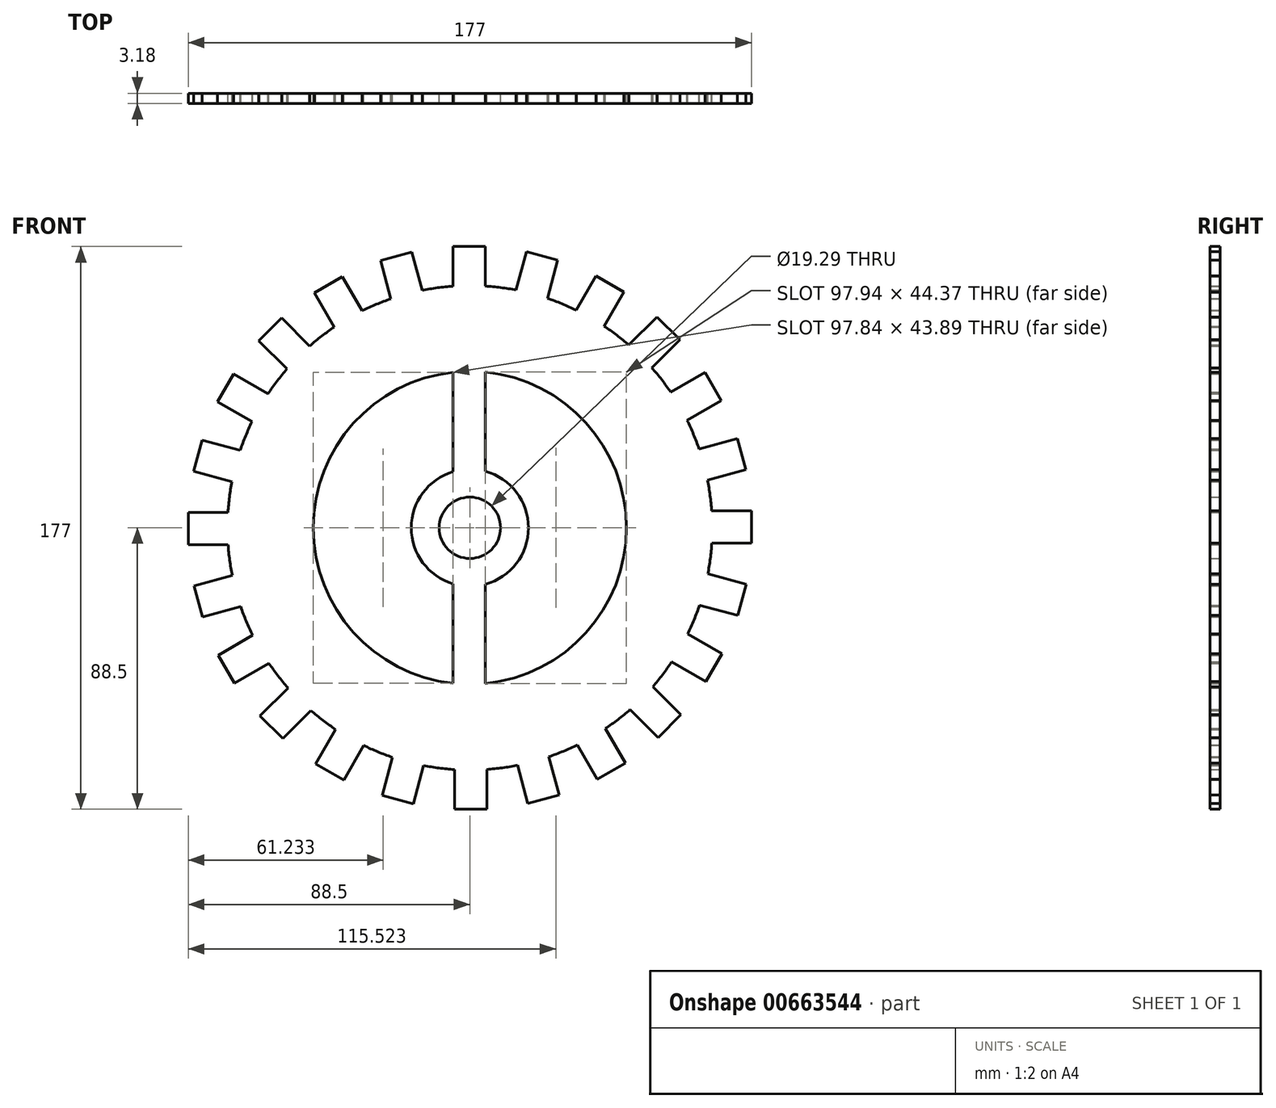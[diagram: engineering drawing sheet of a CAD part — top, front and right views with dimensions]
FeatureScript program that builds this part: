
annotation { "Feature Type Name" : "Feature", "Feature Type Description" : "" }
export const myFeature = defineFeature(function(context is Context, id is Id, definition is map)
    precondition{}
    {
        {
            var Q0;
            Q0=qCreatedBy(makeId("Front.planeOp"),FACE);
            var sketch = newSketch(context, id + "F0", { "sketchPlane" : qUnion([Q0])});
            skCircle(sketch, "E0", {"center": v(0, 0) * mm, "radius": 76.2 * mm, "construction": true});
            skLineSegment(sketch, "E1", {"start": v(-5.32, 76.01) * mm, "end": v(-5.32, 88.5) * mm});
            skLineSegment(sketch, "E2", {"start": v(-5.32, 88.5) * mm, "end": v(4.84, 88.5) * mm});
            skLineSegment(sketch, "E3", {"start": v(4.84, 88.5) * mm, "end": v(4.84, 76.05) * mm});
            skLineSegment(sketch, "E4.1.0", {"start": v(-24.82, 72.05) * mm, "end": v(-28.05, 84.1) * mm});
            skLineSegment(sketch, "E4.1.1", {"start": v(-28.05, 84.1) * mm, "end": v(-18.23, 86.74) * mm});
            skLineSegment(sketch, "E4.1.2", {"start": v(-18.23, 86.74) * mm, "end": v(-15.01, 74.7) * mm});
            skLineSegment(sketch, "E4.2.0", {"start": v(-42.62, 63.17) * mm, "end": v(-48.86, 73.98) * mm});
            skLineSegment(sketch, "E4.2.1", {"start": v(-48.86, 73.98) * mm, "end": v(-40.06, 79.06) * mm});
            skLineSegment(sketch, "E4.2.2", {"start": v(-40.06, 79.06) * mm, "end": v(-33.83, 68.28) * mm});
            skLineSegment(sketch, "E4.3.0", {"start": v(-57.51, 49.99) * mm, "end": v(-66.34, 58.82) * mm});
            skLineSegment(sketch, "E4.3.1", {"start": v(-66.34, 58.82) * mm, "end": v(-59.16, 66) * mm});
            skLineSegment(sketch, "E4.3.2", {"start": v(-59.16, 66) * mm, "end": v(-50.35, 57.2) * mm});
            skLineSegment(sketch, "E4.4.0", {"start": v(-68.5, 33.4) * mm, "end": v(-79.3, 39.64) * mm});
            skLineSegment(sketch, "E4.4.1", {"start": v(-79.3, 39.64) * mm, "end": v(-74.23, 48.44) * mm});
            skLineSegment(sketch, "E4.4.2", {"start": v(-74.23, 48.44) * mm, "end": v(-63.44, 42.21) * mm});
            skLineSegment(sketch, "E4.5.0", {"start": v(-74.8, 14.53) * mm, "end": v(-86.86, 17.76) * mm});
            skLineSegment(sketch, "E4.5.1", {"start": v(-86.86, 17.76) * mm, "end": v(-84.23, 27.58) * mm});
            skLineSegment(sketch, "E4.5.2", {"start": v(-84.23, 27.58) * mm, "end": v(-72.2, 24.35) * mm});
            skLineSegment(sketch, "E4.6.0", {"start": v(-76.01, -5.32) * mm, "end": v(-88.5, -5.32) * mm});
            skLineSegment(sketch, "E4.6.1", {"start": v(-88.5, -5.32) * mm, "end": v(-88.5, 4.84) * mm});
            skLineSegment(sketch, "E4.6.2", {"start": v(-88.5, 4.84) * mm, "end": v(-76.05, 4.84) * mm});
            skLineSegment(sketch, "E4.7.0", {"start": v(-72.05, -24.82) * mm, "end": v(-84.1, -28.05) * mm});
            skLineSegment(sketch, "E4.7.1", {"start": v(-84.1, -28.05) * mm, "end": v(-86.74, -18.23) * mm});
            skLineSegment(sketch, "E4.7.2", {"start": v(-86.74, -18.23) * mm, "end": v(-74.7, -15.01) * mm});
            skLineSegment(sketch, "E4.8.0", {"start": v(-63.17, -42.62) * mm, "end": v(-73.98, -48.86) * mm});
            skLineSegment(sketch, "E4.8.1", {"start": v(-73.98, -48.86) * mm, "end": v(-79.06, -40.06) * mm});
            skLineSegment(sketch, "E4.8.2", {"start": v(-79.06, -40.06) * mm, "end": v(-68.28, -33.83) * mm});
            skLineSegment(sketch, "E4.9.0", {"start": v(-49.99, -57.51) * mm, "end": v(-58.82, -66.34) * mm});
            skLineSegment(sketch, "E4.9.1", {"start": v(-58.82, -66.34) * mm, "end": v(-66, -59.16) * mm});
            skLineSegment(sketch, "E4.9.2", {"start": v(-66, -59.16) * mm, "end": v(-57.2, -50.35) * mm});
            skLineSegment(sketch, "E4.10.0", {"start": v(-33.4, -68.5) * mm, "end": v(-39.64, -79.3) * mm});
            skLineSegment(sketch, "E4.10.1", {"start": v(-39.64, -79.3) * mm, "end": v(-48.44, -74.23) * mm});
            skLineSegment(sketch, "E4.10.2", {"start": v(-48.44, -74.23) * mm, "end": v(-42.21, -63.44) * mm});
            skLineSegment(sketch, "E4.11.0", {"start": v(-14.53, -74.8) * mm, "end": v(-17.76, -86.86) * mm});
            skLineSegment(sketch, "E4.11.1", {"start": v(-17.76, -86.86) * mm, "end": v(-27.58, -84.23) * mm});
            skLineSegment(sketch, "E4.11.2", {"start": v(-27.58, -84.23) * mm, "end": v(-24.35, -72.2) * mm});
            skLineSegment(sketch, "E4.12.0", {"start": v(5.32, -76.01) * mm, "end": v(5.32, -88.5) * mm});
            skLineSegment(sketch, "E4.12.1", {"start": v(5.32, -88.5) * mm, "end": v(-4.84, -88.5) * mm});
            skLineSegment(sketch, "E4.12.2", {"start": v(-4.84, -88.5) * mm, "end": v(-4.84, -76.05) * mm});
            skLineSegment(sketch, "E4.13.0", {"start": v(24.82, -72.05) * mm, "end": v(28.05, -84.1) * mm});
            skLineSegment(sketch, "E4.13.1", {"start": v(28.05, -84.1) * mm, "end": v(18.23, -86.74) * mm});
            skLineSegment(sketch, "E4.13.2", {"start": v(18.23, -86.74) * mm, "end": v(15.01, -74.7) * mm});
            skLineSegment(sketch, "E4.14.0", {"start": v(42.62, -63.17) * mm, "end": v(48.86, -73.98) * mm});
            skLineSegment(sketch, "E4.14.1", {"start": v(48.86, -73.98) * mm, "end": v(40.06, -79.06) * mm});
            skLineSegment(sketch, "E4.14.2", {"start": v(40.06, -79.06) * mm, "end": v(33.83, -68.28) * mm});
            skLineSegment(sketch, "E4.15.0", {"start": v(57.51, -49.99) * mm, "end": v(66.34, -58.82) * mm});
            skLineSegment(sketch, "E4.15.1", {"start": v(66.34, -58.82) * mm, "end": v(59.16, -66) * mm});
            skLineSegment(sketch, "E4.15.2", {"start": v(59.16, -66) * mm, "end": v(50.35, -57.2) * mm});
            skLineSegment(sketch, "E4.16.0", {"start": v(68.5, -33.4) * mm, "end": v(79.3, -39.64) * mm});
            skLineSegment(sketch, "E4.16.1", {"start": v(79.3, -39.64) * mm, "end": v(74.23, -48.44) * mm});
            skLineSegment(sketch, "E4.16.2", {"start": v(74.23, -48.44) * mm, "end": v(63.44, -42.21) * mm});
            skLineSegment(sketch, "E4.17.0", {"start": v(74.8, -14.53) * mm, "end": v(86.86, -17.76) * mm});
            skLineSegment(sketch, "E4.17.1", {"start": v(86.86, -17.76) * mm, "end": v(84.23, -27.58) * mm});
            skLineSegment(sketch, "E4.17.2", {"start": v(84.23, -27.58) * mm, "end": v(72.2, -24.35) * mm});
            skLineSegment(sketch, "E4.18.0", {"start": v(76.01, 5.32) * mm, "end": v(88.5, 5.32) * mm});
            skLineSegment(sketch, "E4.18.1", {"start": v(88.5, 5.32) * mm, "end": v(88.5, -4.84) * mm});
            skLineSegment(sketch, "E4.18.2", {"start": v(88.5, -4.84) * mm, "end": v(76.05, -4.84) * mm});
            skLineSegment(sketch, "E4.19.0", {"start": v(72.05, 24.82) * mm, "end": v(84.1, 28.05) * mm});
            skLineSegment(sketch, "E4.19.1", {"start": v(84.1, 28.05) * mm, "end": v(86.74, 18.23) * mm});
            skLineSegment(sketch, "E4.19.2", {"start": v(86.74, 18.23) * mm, "end": v(74.7, 15.01) * mm});
            skLineSegment(sketch, "E4.20.0", {"start": v(63.17, 42.62) * mm, "end": v(73.98, 48.86) * mm});
            skLineSegment(sketch, "E4.20.1", {"start": v(73.98, 48.86) * mm, "end": v(79.06, 40.06) * mm});
            skLineSegment(sketch, "E4.20.2", {"start": v(79.06, 40.06) * mm, "end": v(68.28, 33.83) * mm});
            skLineSegment(sketch, "E4.21.0", {"start": v(49.99, 57.51) * mm, "end": v(58.82, 66.34) * mm});
            skLineSegment(sketch, "E4.21.1", {"start": v(58.82, 66.34) * mm, "end": v(66, 59.16) * mm});
            skLineSegment(sketch, "E4.21.2", {"start": v(66, 59.16) * mm, "end": v(57.2, 50.35) * mm});
            skLineSegment(sketch, "E4.22.0", {"start": v(33.4, 68.5) * mm, "end": v(39.64, 79.3) * mm});
            skLineSegment(sketch, "E4.22.1", {"start": v(39.64, 79.3) * mm, "end": v(48.44, 74.23) * mm});
            skLineSegment(sketch, "E4.22.2", {"start": v(48.44, 74.23) * mm, "end": v(42.21, 63.44) * mm});
            skLineSegment(sketch, "E4.23.0", {"start": v(14.53, 74.8) * mm, "end": v(17.76, 86.86) * mm});
            skLineSegment(sketch, "E4.23.1", {"start": v(17.76, 86.86) * mm, "end": v(27.58, 84.23) * mm});
            skLineSegment(sketch, "E4.23.2", {"start": v(27.58, 84.23) * mm, "end": v(24.35, 72.2) * mm});
            skCircle(sketch, "E5", {"center": v(0, 0) * mm, "radius": 18.42 * mm});
            skCircle(sketch, "E6", {"center": v(0, 0) * mm, "radius": 49.2 * mm});
            skCircle(sketch, "E7", {"center": v(0, 0) * mm, "radius": 76.2 * mm});
            skLineSegment(sketch, "E8", {"start": v(-5.32, 48.92) * mm, "end": v(-5.32, 17.63) * mm});
            skLineSegment(sketch, "E9", {"start": v(4.84, 48.97) * mm, "end": v(4.84, 17.77) * mm});
            skLineSegment(sketch, "E10", {"start": v(-5.32, -17.63) * mm, "end": v(-5.32, -48.92) * mm});
            skLineSegment(sketch, "E11", {"start": v(4.84, -17.77) * mm, "end": v(4.84, -48.97) * mm});
            skCircle(sketch, "E12", {"center": v(0, 0) * mm, "radius": 9.65 * mm});
            skSolve(sketch);
        }
        {
            var Q0;
            {var subQ0=sQuery(id+"F0.wireOp",EDGE,"E5");var subQ1=makeQuery(id+"F0.imprint","INTERSECT",VERTEX,{"derivedFrom":[subQ0,sQuery(id+"F0.wireOp",EDGE,"E8")]});Q0=makeQuery(id+"F0.imprint","IMPRINT",FACE,{"disambiguationData":[TD([[makeQuery(id+"F0.imprint","IMPRINT",EDGE,{"disambiguationData":[TD([[subQ1,1.0]])],"derivedFrom":subQ0}),1.0]])]});}
            var Q1;
            {var subQ0=sQuery(id+"F0.wireOp",EDGE,"E8");Q1=makeQuery(id+"F0.imprint","IMPRINT",FACE,{"disambiguationData":[TD([[makeQuery(id+"F0.imprint","IMPRINT",EDGE,{"derivedFrom":subQ0}),1.0]])]});}
            var Q2;
            {var subQ0=sQuery(id+"F0.wireOp",EDGE,"E10");Q2=makeQuery(id+"F0.imprint","IMPRINT",FACE,{"disambiguationData":[TD([[makeQuery(id+"F0.imprint","IMPRINT",EDGE,{"derivedFrom":subQ0}),1.0]])]});}
            var Q3;
            {var subQ33=sQuery(id+"F0.wireOp",EDGE,"E6");var subQ34=makeQuery(id+"F0.imprint","INTERSECT",VERTEX,{"derivedFrom":[subQ33,sQuery(id+"F0.wireOp",EDGE,"E8")]});Q3=makeQuery(id+"F0.imprint","IMPRINT",FACE,{"disambiguationData":[TD([[makeQuery(id+"F0.imprint","IMPRINT",EDGE,{"disambiguationData":[TD([[subQ34,1.0]])],"derivedFrom":subQ33}),-1.0]])]});}
            var Q4;
            {var subQ0=sQuery(id+"F0.wireOp",EDGE,"E4.12.0");Q4=makeQuery(id+"F0.imprint","IMPRINT",FACE,{"disambiguationData":[TD([[makeQuery(id+"F0.imprint","IMPRINT",EDGE,{"derivedFrom":subQ0}),-1.0]])]});}
            var Q5;
            {var subQ0=sQuery(id+"F0.wireOp",EDGE,"E4.13.0");Q5=makeQuery(id+"F0.imprint","IMPRINT",FACE,{"disambiguationData":[TD([[makeQuery(id+"F0.imprint","IMPRINT",EDGE,{"derivedFrom":subQ0}),-1.0]])]});}
            var Q6;
            {var subQ0=sQuery(id+"F0.wireOp",EDGE,"E4.14.0");Q6=makeQuery(id+"F0.imprint","IMPRINT",FACE,{"disambiguationData":[TD([[makeQuery(id+"F0.imprint","IMPRINT",EDGE,{"derivedFrom":subQ0}),-1.0]])]});}
            var Q7;
            {var subQ0=sQuery(id+"F0.wireOp",EDGE,"E4.15.0");Q7=makeQuery(id+"F0.imprint","IMPRINT",FACE,{"disambiguationData":[TD([[makeQuery(id+"F0.imprint","IMPRINT",EDGE,{"derivedFrom":subQ0}),-1.0]])]});}
            var Q8;
            {var subQ0=sQuery(id+"F0.wireOp",EDGE,"E4.16.0");Q8=makeQuery(id+"F0.imprint","IMPRINT",FACE,{"disambiguationData":[TD([[makeQuery(id+"F0.imprint","IMPRINT",EDGE,{"derivedFrom":subQ0}),-1.0]])]});}
            var Q9;
            {var subQ0=sQuery(id+"F0.wireOp",EDGE,"E4.17.0");Q9=makeQuery(id+"F0.imprint","IMPRINT",FACE,{"disambiguationData":[TD([[makeQuery(id+"F0.imprint","IMPRINT",EDGE,{"derivedFrom":subQ0}),-1.0]])]});}
            var Q10;
            {var subQ0=sQuery(id+"F0.wireOp",EDGE,"E4.18.0");Q10=makeQuery(id+"F0.imprint","IMPRINT",FACE,{"disambiguationData":[TD([[makeQuery(id+"F0.imprint","IMPRINT",EDGE,{"derivedFrom":subQ0}),-1.0]])]});}
            var Q11;
            {var subQ0=sQuery(id+"F0.wireOp",EDGE,"E4.19.0");Q11=makeQuery(id+"F0.imprint","IMPRINT",FACE,{"disambiguationData":[TD([[makeQuery(id+"F0.imprint","IMPRINT",EDGE,{"derivedFrom":subQ0}),-1.0]])]});}
            var Q12;
            {var subQ0=sQuery(id+"F0.wireOp",EDGE,"E4.20.0");Q12=makeQuery(id+"F0.imprint","IMPRINT",FACE,{"disambiguationData":[TD([[makeQuery(id+"F0.imprint","IMPRINT",EDGE,{"derivedFrom":subQ0}),-1.0]])]});}
            var Q13;
            {var subQ0=sQuery(id+"F0.wireOp",EDGE,"E4.22.0");Q13=makeQuery(id+"F0.imprint","IMPRINT",FACE,{"disambiguationData":[TD([[makeQuery(id+"F0.imprint","IMPRINT",EDGE,{"derivedFrom":subQ0}),-1.0]])]});}
            var Q14;
            {var subQ0=sQuery(id+"F0.wireOp",EDGE,"E4.23.0");Q14=makeQuery(id+"F0.imprint","IMPRINT",FACE,{"disambiguationData":[TD([[makeQuery(id+"F0.imprint","IMPRINT",EDGE,{"derivedFrom":subQ0}),-1.0]])]});}
            var Q15;
            {var subQ0=sQuery(id+"F0.wireOp",EDGE,"E4.21.0");Q15=makeQuery(id+"F0.imprint","IMPRINT",FACE,{"disambiguationData":[TD([[makeQuery(id+"F0.imprint","IMPRINT",EDGE,{"derivedFrom":subQ0}),-1.0]])]});}
            var Q16;
            {var subQ0=sQuery(id+"F0.wireOp",EDGE,"E1");Q16=makeQuery(id+"F0.imprint","IMPRINT",FACE,{"disambiguationData":[TD([[makeQuery(id+"F0.imprint","IMPRINT",EDGE,{"derivedFrom":subQ0}),-1.0]])]});}
            var Q17;
            {var subQ0=sQuery(id+"F0.wireOp",EDGE,"E4.1.0");Q17=makeQuery(id+"F0.imprint","IMPRINT",FACE,{"disambiguationData":[TD([[makeQuery(id+"F0.imprint","IMPRINT",EDGE,{"derivedFrom":subQ0}),-1.0]])]});}
            var Q18;
            {var subQ0=sQuery(id+"F0.wireOp",EDGE,"E4.2.0");Q18=makeQuery(id+"F0.imprint","IMPRINT",FACE,{"disambiguationData":[TD([[makeQuery(id+"F0.imprint","IMPRINT",EDGE,{"derivedFrom":subQ0}),-1.0]])]});}
            var Q19;
            {var subQ0=sQuery(id+"F0.wireOp",EDGE,"E4.3.0");Q19=makeQuery(id+"F0.imprint","IMPRINT",FACE,{"disambiguationData":[TD([[makeQuery(id+"F0.imprint","IMPRINT",EDGE,{"derivedFrom":subQ0}),-1.0]])]});}
            var Q20;
            {var subQ0=sQuery(id+"F0.wireOp",EDGE,"E4.4.0");Q20=makeQuery(id+"F0.imprint","IMPRINT",FACE,{"disambiguationData":[TD([[makeQuery(id+"F0.imprint","IMPRINT",EDGE,{"derivedFrom":subQ0}),-1.0]])]});}
            var Q21;
            {var subQ0=sQuery(id+"F0.wireOp",EDGE,"E4.5.0");Q21=makeQuery(id+"F0.imprint","IMPRINT",FACE,{"disambiguationData":[TD([[makeQuery(id+"F0.imprint","IMPRINT",EDGE,{"derivedFrom":subQ0}),-1.0]])]});}
            var Q22;
            {var subQ0=sQuery(id+"F0.wireOp",EDGE,"E4.6.0");Q22=makeQuery(id+"F0.imprint","IMPRINT",FACE,{"disambiguationData":[TD([[makeQuery(id+"F0.imprint","IMPRINT",EDGE,{"derivedFrom":subQ0}),-1.0]])]});}
            var Q23;
            {var subQ0=sQuery(id+"F0.wireOp",EDGE,"E4.7.0");Q23=makeQuery(id+"F0.imprint","IMPRINT",FACE,{"disambiguationData":[TD([[makeQuery(id+"F0.imprint","IMPRINT",EDGE,{"derivedFrom":subQ0}),-1.0]])]});}
            var Q24;
            {var subQ0=sQuery(id+"F0.wireOp",EDGE,"E4.8.0");Q24=makeQuery(id+"F0.imprint","IMPRINT",FACE,{"disambiguationData":[TD([[makeQuery(id+"F0.imprint","IMPRINT",EDGE,{"derivedFrom":subQ0}),-1.0]])]});}
            var Q25;
            {var subQ0=sQuery(id+"F0.wireOp",EDGE,"E4.9.0");Q25=makeQuery(id+"F0.imprint","IMPRINT",FACE,{"disambiguationData":[TD([[makeQuery(id+"F0.imprint","IMPRINT",EDGE,{"derivedFrom":subQ0}),-1.0]])]});}
            var Q26;
            {var subQ0=sQuery(id+"F0.wireOp",EDGE,"E4.10.0");Q26=makeQuery(id+"F0.imprint","IMPRINT",FACE,{"disambiguationData":[TD([[makeQuery(id+"F0.imprint","IMPRINT",EDGE,{"derivedFrom":subQ0}),-1.0]])]});}
            var Q27;
            {var subQ0=sQuery(id+"F0.wireOp",EDGE,"E4.11.0");Q27=makeQuery(id+"F0.imprint","IMPRINT",FACE,{"disambiguationData":[TD([[makeQuery(id+"F0.imprint","IMPRINT",EDGE,{"derivedFrom":subQ0}),-1.0]])]});}
            extrude(context, id + "F1", {"entities" : qUnion([Q0, Q1, Q2, Q3, Q4, Q5, Q6, Q7, Q8, Q9, Q10, Q11, Q12, Q13, Q14, Q15, Q16, Q17, Q18, Q19, Q20, Q21, Q22, Q23, Q24, Q25, Q26, Q27]), "depth" : 3.17 * mm, "offsetDistance" : 25.4 * mm});
        }
    });
